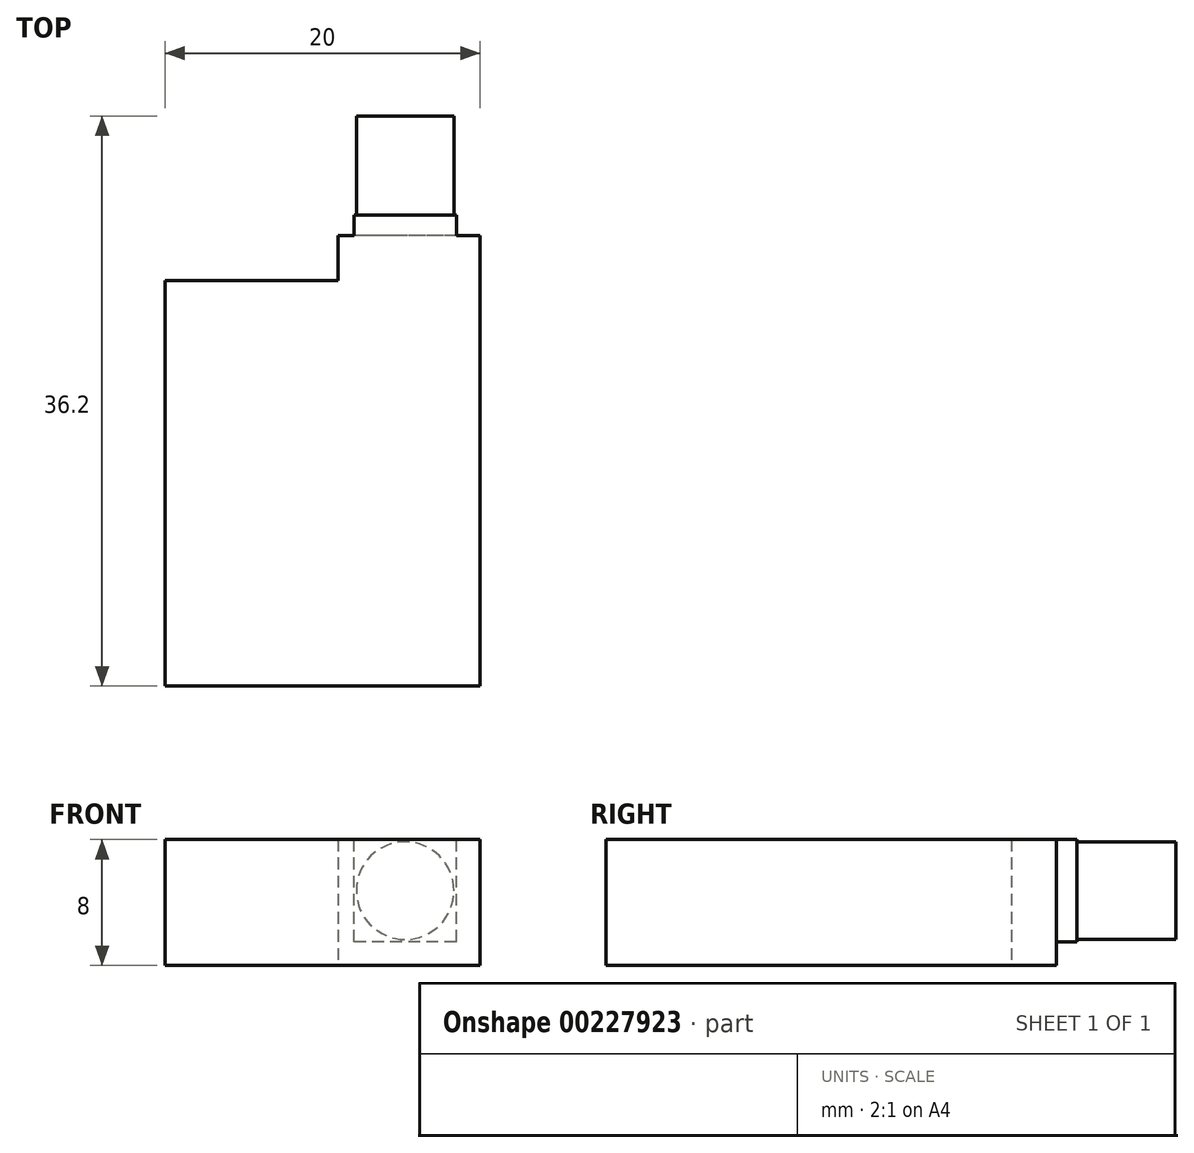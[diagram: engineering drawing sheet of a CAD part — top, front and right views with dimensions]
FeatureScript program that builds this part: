
annotation { "Feature Type Name" : "Feature", "Feature Type Description" : "" }
export const myFeature = defineFeature(function(context is Context, id is Id, definition is map)
    precondition{}
    {
        {
            var Q0;
            Q0=qCreatedBy(makeId("Top.planeOp"),FACE);
            var sketch = newSketch(context, id + "F0", { "sketchPlane" : qUnion([Q0])});
            skLineSegment(sketch, "E0.bottom", {"start": v(-11.43, 6.16) * mm, "end": v(-0.43, 6.16) * mm});
            skLineSegment(sketch, "E0.top", {"start": v(-11.43, -19.6) * mm, "end": v(8.57, -19.6) * mm});
            skLineSegment(sketch, "E0.left", {"start": v(-11.43, 6.16) * mm, "end": v(-11.43, -19.6) * mm});
            skLineSegment(sketch, "E0.right", {"start": v(8.57, 6.16) * mm, "end": v(8.57, -19.6) * mm});
            skLineSegment(sketch, "E1.top", {"start": v(8.57, 9) * mm, "end": v(-0.43, 9) * mm});
            skLineSegment(sketch, "E1.left", {"start": v(8.57, 6.16) * mm, "end": v(8.57, 9) * mm});
            skLineSegment(sketch, "E1.right", {"start": v(-0.43, 6.16) * mm, "end": v(-0.43, 9) * mm});
            skSolve(sketch);
        }
        {
            var Q0;
            Q0=makeQuery(id+"F0.imprint","IMPRINT",FACE,{"disambiguationData":[TD([[makeQuery(id+"F0.imprint","IMPRINT",EDGE,{"derivedFrom":sQuery(id+"F0.wireOp",EDGE,"E0.bottom")}),-1.0]])]});
            extrude(context, id + "F1", {"entities" : qUnion([Q0]), "depth" : 8 * mm});
        }
        {
            var Q0;
            Q0=makeQuery(id+"F1.opExtrude","SWEPT_FACE",FACE,{"disambiguationData":[OSD([sQuery(id+"F0.wireOp",EDGE,"E1.top")])]});
            var sketch = newSketch(context, id + "F2", { "sketchPlane" : qUnion([Q0])});
            skLineSegment(sketch, "E2.bottom", {"start": v(-7.07, 1.5) * mm, "end": v(-0.57, 1.5) * mm});
            skLineSegment(sketch, "E2.top", {"start": v(-7.07, 8) * mm, "end": v(-0.57, 8) * mm});
            skLineSegment(sketch, "E2.left", {"start": v(-7.07, 1.5) * mm, "end": v(-7.07, 8) * mm});
            skLineSegment(sketch, "E2.right", {"start": v(-0.57, 1.5) * mm, "end": v(-0.57, 8) * mm});
            skSolve(sketch);
        }
        {
            var Q0;
            Q0=makeQuery(id+"F2.imprint","IMPRINT",FACE,{"disambiguationData":[TD([[makeQuery(id+"F2.imprint","IMPRINT",EDGE,{"derivedFrom":sQuery(id+"F2.wireOp",EDGE,"E2.bottom")}),1.0]])]});
            extrude(context, id + "F3", {"entities" : qUnion([Q0]), "operationType" : NewBodyOperationType.ADD, "depth" : 1.3 * mm});
        }
        {
            var Q0;
            Q0=makeQuery(id+"F3.opExtrude","CAP_FACE",FACE,{"disambiguationData":[OSD([sQuery(id+"F2.wireOp",EDGE,"E2.bottom"),sQuery(id+"F2.wireOp",EDGE,"E2.top"),sQuery(id+"F2.wireOp",EDGE,"E2.left"),sQuery(id+"F2.wireOp",EDGE,"E2.right")])],"isStart":false});
            var sketch = newSketch(context, id + "F4", { "sketchPlane" : qUnion([Q0])});
            skCircle(sketch, "E3", {"center": v(-3.82, 4.75) * mm, "radius": 3.1 * mm});
            skLineSegment(sketch, "E4", {"start": v(-7.07, 1.5) * mm, "end": v(-0.57, 8) * mm, "construction": true});
            skSolve(sketch);
        }
        {
            var Q0;
            Q0 = qSketchRegion(id + "F4", true);
            extrude(context, id + "F5", {"entities" : qUnion([Q0]), "operationType" : NewBodyOperationType.ADD, "depth" : 6.3 * mm});
        }
    });
